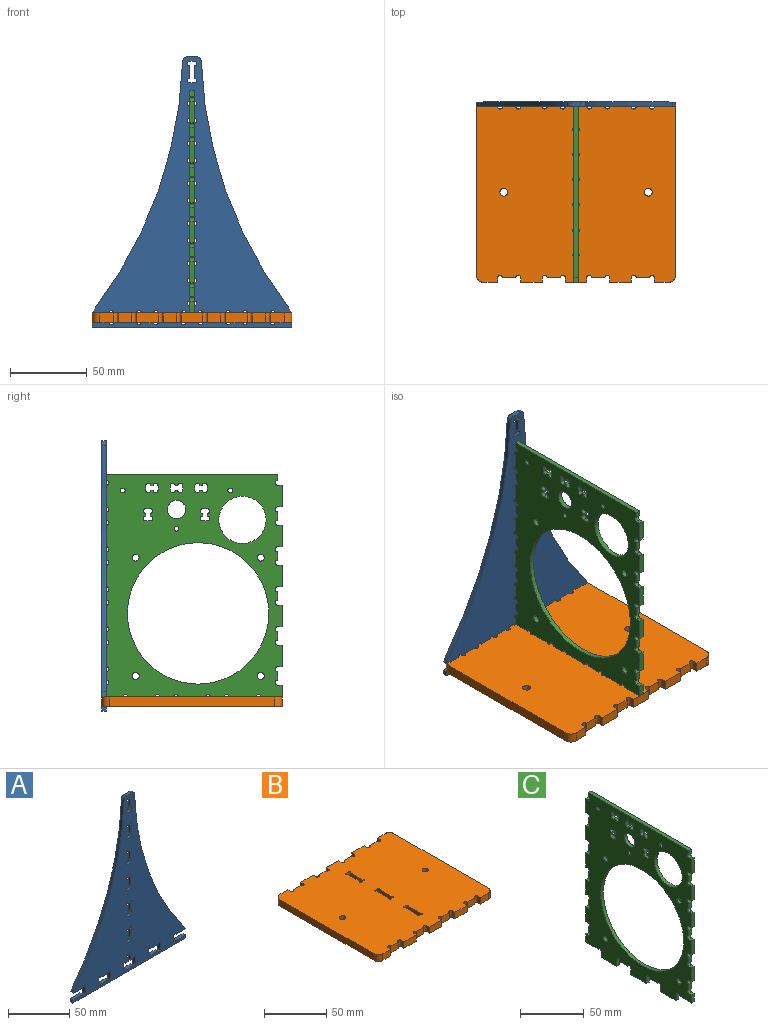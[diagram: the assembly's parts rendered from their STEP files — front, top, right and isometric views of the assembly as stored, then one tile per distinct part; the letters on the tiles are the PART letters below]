
ASSEMBLY  parts=3 mates=1
PART A: 100 faces, bbox 130x3x176 mm
  f0: plane 176x130mm, normal (0,-1,0), area 8856mm2, adj f2,f3,f4,f5,f6,f7,f8,f9
  f1: plane 176x130mm, normal (0,1,0), area 8856mm2, adj f2,f3,f4,f5,f6,f7,f8,f9
  f2: plane 3x2.5mm, normal (0,0,-1), area 7.5mm2, adj f0,f1,f19,f57
  f3: plane 11x3mm, normal (0,0,1), area 33mm2, adj f0,f1,f6,f46
  f4: plane 10.61x3mm, normal (0,0,-1), area 31.8mm2, adj f0,f1,f14,f45
  f5: cylinder r=10mm len=3.3mm, axis (0,1,0), area 11.1mm2, adj f0,f1,f9,f41
  f6: plane 3x3mm, normal (-1,0,0), area 9mm2, adj f0,f1,f3,f7
  f7: plane 130x3mm, normal (0,0,-1), area 390mm2, adj f0,f1,f6,f8
  f8: plane 3x3mm, normal (1,0,0), area 9mm2, adj f0,f1,f7,f40
  f9: cylinder r=280mm len=160.45mm, axis (0,1,0), area 518.9mm2, adj f0,f1,f5,f13
  f10: plane 6.16x3mm, normal (0,0,1), area 18.5mm2, adj f0,f1,f12,f13
  f11: cylinder r=280mm len=160.45mm, axis (0,1,0), area 518.9mm2, adj f0,f1,f12,f14
  f12: cylinder r=3mm len=3mm, axis (0,1,0), area 13.9mm2, adj f0,f1,f10,f11
  f13: cylinder r=3mm len=3mm, axis (0,1,0), area 13.9mm2, adj f0,f1,f9,f10
  f14: cylinder r=10mm len=3.3mm, axis (0,1,0), area 11.1mm2, adj f0,f1,f4,f11
  f15: plane 8x3mm, normal (0,0,1), area 24mm2, adj f0,f1,f20,f22
  f16: plane 6.35x3mm, normal (-1,0,0), area 19.1mm2, adj f0,f1,f21,f22
  f17: plane 3x2.5mm, normal (0,0,-1), area 7.5mm2, adj f0,f1,f21,f56
  f18: plane 6.35x3mm, normal (1,0,0), area 19.1mm2, adj f0,f1,f19,f20
  f19: cylinder r=1.5mm len=3mm, axis (0,-1,0), area 14.1mm2, adj f0,f1,f2,f18
  f20: cylinder r=1.5mm len=3mm, axis (0,-1,0), area 14.1mm2, adj f0,f1,f15,f18
  f21: cylinder r=1.5mm len=3mm, axis (0,-1,0), area 14.1mm2, adj f0,f1,f16,f17
  f22: cylinder r=1.5mm len=3mm, axis (0,-1,0), area 14.1mm2, adj f0,f1,f15,f16
  f23: plane 8x3mm, normal (0,0,1), area 24mm2, adj f0,f1,f28,f30
  f24: plane 6.35x3mm, normal (-1,0,0), area 19.1mm2, adj f0,f1,f29,f30
  f25: plane 8x3mm, normal (0,0,-1), area 24mm2, adj f0,f1,f27,f29
  f26: plane 6.35x3mm, normal (1,0,0), area 19.1mm2, adj f0,f1,f27,f28
  f27: cylinder r=1.5mm len=3mm, axis (0,-1,0), area 14.1mm2, adj f0,f1,f25,f26
  f28: cylinder r=1.5mm len=3mm, axis (0,-1,0), area 14.1mm2, adj f0,f1,f23,f26
  f29: cylinder r=1.5mm len=3mm, axis (0,-1,0), area 14.1mm2, adj f0,f1,f24,f25
  f30: cylinder r=1.5mm len=3mm, axis (0,-1,0), area 14.1mm2, adj f0,f1,f23,f24
  f31: plane 8x3mm, normal (0,0,1), area 24mm2, adj f0,f1,f36,f38
  f32: plane 6.35x3mm, normal (-1,0,0), area 19.1mm2, adj f0,f1,f37,f38
  f33: plane 8x3mm, normal (0,0,-1), area 24mm2, adj f0,f1,f35,f37
  f34: plane 6.35x3mm, normal (1,0,0), area 19.1mm2, adj f0,f1,f35,f36
  f35: cylinder r=1.5mm len=3mm, axis (0,-1,0), area 14.1mm2, adj f0,f1,f33,f34
  f36: cylinder r=1.5mm len=3mm, axis (0,-1,0), area 14.1mm2, adj f0,f1,f31,f34
  f37: cylinder r=1.5mm len=3mm, axis (0,-1,0), area 14.1mm2, adj f0,f1,f32,f33
  f38: cylinder r=1.5mm len=3mm, axis (0,-1,0), area 14.1mm2, adj f0,f1,f31,f32
  f39: plane 6.35x3mm, normal (1,0,0), area 19.1mm2, adj f0,f1,f42,f43
  f40: plane 11x3mm, normal (0,0,1), area 33mm2, adj f0,f1,f8,f43
  f41: plane 10.61x3mm, normal (0,0,-1), area 31.8mm2, adj f0,f1,f5,f42
  f42: cylinder r=1.5mm len=3mm, axis (0,-1,0), area 14.1mm2, adj f0,f1,f39,f41
  f43: cylinder r=1.5mm len=3mm, axis (0,-1,0), area 14.1mm2, adj f0,f1,f39,f40
  f44: plane 6.35x3mm, normal (-1,0,0), area 19.1mm2, adj f0,f1,f45,f46
  f45: cylinder r=1.5mm len=3mm, axis (0,-1,0), area 14.1mm2, adj f0,f1,f4,f44
  f46: cylinder r=1.5mm len=3mm, axis (0,-1,0), area 14.1mm2, adj f0,f1,f3,f44
  f47: plane 3x3mm, normal (0,0,1), area 9mm2, adj f0,f1,f51,f54
  f48: plane 8x3mm, normal (-1,0,0), area 24mm2, adj f0,f1,f52,f54
  f49: plane 3x3mm, normal (0,0,-1), area 9mm2, adj f0,f1,f52,f53
  f50: plane 8x3mm, normal (1,0,0), area 24mm2, adj f0,f1,f51,f53
  f51: cylinder r=1.5mm len=3mm, axis (0,-1,0), area 14.1mm2, adj f0,f1,f47,f50
  f52: cylinder r=1.5mm len=3mm, axis (0,-1,0), area 14.1mm2, adj f0,f1,f48,f49
  f53: cylinder r=1.5mm len=3mm, axis (0,-1,0), area 14.1mm2, adj f0,f1,f49,f50
  f54: cylinder r=1.5mm len=3mm, axis (0,-1,0), area 14.1mm2, adj f0,f1,f47,f48
  f55: plane 3x3mm, normal (0,0,-1), area 9mm2, adj f0,f1,f58,f59
  f56: plane 4.65x3mm, normal (-1,0,0), area 14mm2, adj f0,f1,f17,f58
  f57: plane 4.65x3mm, normal (1,0,0), area 14mm2, adj f0,f1,f2,f59
  f58: cylinder r=1.5mm len=3mm, axis (0,-1,0), area 14.1mm2, adj f0,f1,f55,f56
  f59: cylinder r=1.5mm len=3mm, axis (0,-1,0), area 14.1mm2, adj f0,f1,f55,f57
  f60: plane 3x3mm, normal (0,0,1), area 9mm2, adj f0,f1,f64,f67
  f61: plane 8x3mm, normal (-1,0,0), area 24mm2, adj f0,f1,f65,f67
  f62: plane 3x3mm, normal (0,0,-1), area 9mm2, adj f0,f1,f65,f66
  f63: plane 8x3mm, normal (1,0,0), area 24mm2, adj f0,f1,f64,f66
  f64: cylinder r=1.5mm len=3mm, axis (0,-1,0), area 14.1mm2, adj f0,f1,f60,f63
  f65: cylinder r=1.5mm len=3mm, axis (0,-1,0), area 14.1mm2, adj f0,f1,f61,f62
  f66: cylinder r=1.5mm len=3mm, axis (0,-1,0), area 14.1mm2, adj f0,f1,f62,f63
  f67: cylinder r=1.5mm len=3mm, axis (0,-1,0), area 14.1mm2, adj f0,f1,f60,f61
  f68: plane 3x3mm, normal (0,0,1), area 9mm2, adj f0,f1,f72,f75
  f69: plane 8x3mm, normal (-1,0,0), area 24mm2, adj f0,f1,f73,f75
  f70: plane 3x3mm, normal (0,0,-1), area 9mm2, adj f0,f1,f73,f74
  f71: plane 8x3mm, normal (1,0,0), area 24mm2, adj f0,f1,f72,f74
  f72: cylinder r=1.5mm len=3mm, axis (0,-1,0), area 14.1mm2, adj f0,f1,f68,f71
  f73: cylinder r=1.5mm len=3mm, axis (0,-1,0), area 14.1mm2, adj f0,f1,f69,f70
  f74: cylinder r=1.5mm len=3mm, axis (0,-1,0), area 14.1mm2, adj f0,f1,f70,f71
  f75: cylinder r=1.5mm len=3mm, axis (0,-1,0), area 14.1mm2, adj f0,f1,f68,f69
  f76: plane 3x3mm, normal (0,0,1), area 9mm2, adj f0,f1,f80,f83
  f77: plane 8x3mm, normal (-1,0,0), area 24mm2, adj f0,f1,f81,f83
  f78: plane 3x3mm, normal (0,0,-1), area 9mm2, adj f0,f1,f81,f82
  f79: plane 8x3mm, normal (1,0,0), area 24mm2, adj f0,f1,f80,f82
  f80: cylinder r=1.5mm len=3mm, axis (0,-1,0), area 14.1mm2, adj f0,f1,f76,f79
  f81: cylinder r=1.5mm len=3mm, axis (0,-1,0), area 14.1mm2, adj f0,f1,f77,f78
  f82: cylinder r=1.5mm len=3mm, axis (0,-1,0), area 14.1mm2, adj f0,f1,f78,f79
  f83: cylinder r=1.5mm len=3mm, axis (0,-1,0), area 14.1mm2, adj f0,f1,f76,f77
  f84: plane 3x3mm, normal (0,0,1), area 9mm2, adj f0,f1,f88,f91
  f85: plane 8x3mm, normal (-1,0,0), area 24mm2, adj f0,f1,f89,f91
  f86: plane 3x3mm, normal (0,0,-1), area 9mm2, adj f0,f1,f89,f90
  f87: plane 8x3mm, normal (1,0,0), area 24mm2, adj f0,f1,f88,f90
  f88: cylinder r=1.5mm len=3mm, axis (0,-1,0), area 14.1mm2, adj f0,f1,f84,f87
  f89: cylinder r=1.5mm len=3mm, axis (0,-1,0), area 14.1mm2, adj f0,f1,f85,f86
  f90: cylinder r=1.5mm len=3mm, axis (0,-1,0), area 14.1mm2, adj f0,f1,f86,f87
  f91: cylinder r=1.5mm len=3mm, axis (0,-1,0), area 14.1mm2, adj f0,f1,f84,f85
  f92: plane 3x3mm, normal (0,0,1), area 9mm2, adj f0,f1,f96,f99
  f93: plane 8x3mm, normal (-1,0,0), area 24mm2, adj f0,f1,f97,f99
  f94: plane 3x3mm, normal (0,0,-1), area 9mm2, adj f0,f1,f97,f98
  f95: plane 8x3mm, normal (1,0,0), area 24mm2, adj f0,f1,f96,f98
  f96: cylinder r=1.5mm len=3mm, axis (0,-1,0), area 14.1mm2, adj f0,f1,f92,f95
  f97: cylinder r=1.5mm len=3mm, axis (0,-1,0), area 14.1mm2, adj f0,f1,f93,f94
  f98: cylinder r=1.5mm len=3mm, axis (0,-1,0), area 14.1mm2, adj f0,f1,f94,f95
  f99: cylinder r=1.5mm len=3mm, axis (0,-1,0), area 14.1mm2, adj f0,f1,f92,f93
PART B: 84 faces, bbox 130x117.4x6.4 mm
  f0: plane 130x117.4mm, normal (0,0,1), area 14605.3mm2, adj f2,f3,f4,f5,f6,f7,f8,f9
  f1: plane 130x117.4mm, normal (0,0,-1), area 14605.3mm2, adj f2,f3,f4,f5,f6,f7,f8,f9
  f2: plane 9x6.35mm, normal (0,-1,0), area 57.1mm2, adj f0,f1,f47,f80
  f3: plane 14x6.35mm, normal (0,-1,0), area 88.9mm2, adj f0,f1,f44,f49
  f4: plane 8.65x6.35mm, normal (0,-1,0), area 54.9mm2, adj f0,f1,f42,f43
  f5: plane 8.65x6.35mm, normal (0,-1,0), area 54.9mm2, adj f0,f1,f40,f41
  f6: plane 14x6.35mm, normal (0,-1,0), area 88.9mm2, adj f0,f1,f37,f38
  f7: plane 14x6.35mm, normal (0,-1,0), area 88.9mm2, adj f0,f1,f36,f46
  f8: plane 8.65x6.35mm, normal (0,1,0), area 54.9mm2, adj f0,f1,f34,f35
  f9: plane 8.65x6.35mm, normal (0,1,0), area 54.9mm2, adj f0,f1,f32,f33
  f10: plane 9x6.35mm, normal (0,1,0), area 57.1mm2, adj f0,f1,f31,f81
  f11: plane 14x6.35mm, normal (0,1,0), area 88.9mm2, adj f0,f1,f29,f30
  f12: plane 14x6.35mm, normal (0,1,0), area 88.9mm2, adj f0,f1,f18,f23
  f13: plane 14x6.35mm, normal (0,1,0), area 88.9mm2, adj f0,f1,f20,f28
  f14: plane 9x6.35mm, normal (0,-1,0), area 57.1mm2, adj f0,f1,f39,f83
  f15: plane 107.4x6.35mm, normal (1,0,0), area 682mm2, adj f0,f1,f80,f81
  f16: plane 9x6.35mm, normal (0,1,0), area 57.1mm2, adj f0,f1,f21,f82
  f17: plane 107.4x6.35mm, normal (-1,0,0), area 682mm2, adj f0,f1,f82,f83
  f18: plane 6.35x3mm, normal (1,0,0), area 19mm2, adj f0,f1,f12,f27
  f19: plane 8.65x6.35mm, normal (0,1,0), area 54.9mm2, adj f0,f1,f26,f27
  f20: plane 6.35x3mm, normal (-1,0,0), area 19mm2, adj f0,f1,f13,f26
  f21: plane 6.35x3mm, normal (1,0,0), area 19mm2, adj f0,f1,f16,f25
  f22: plane 8.65x6.35mm, normal (0,1,0), area 54.9mm2, adj f0,f1,f24,f25
  f23: plane 6.35x3mm, normal (-1,0,0), area 19mm2, adj f0,f1,f12,f24
  f24: cylinder r=1.59mm len=6.35mm, axis (0,0,1), area 31.7mm2, adj f0,f1,f22,f23
  f25: cylinder r=1.59mm len=6.35mm, axis (0,0,1), area 31.7mm2, adj f0,f1,f21,f22
  f26: cylinder r=1.59mm len=6.35mm, axis (0,0,1), area 31.7mm2, adj f0,f1,f19,f20
  f27: cylinder r=1.59mm len=6.35mm, axis (0,0,1), area 31.7mm2, adj f0,f1,f18,f19
  f28: plane 6.35x3mm, normal (1,0,0), area 19mm2, adj f0,f1,f13,f35
  f29: plane 6.35x3mm, normal (-1,0,0), area 19mm2, adj f0,f1,f11,f34
  f30: plane 6.35x3mm, normal (1,0,0), area 19mm2, adj f0,f1,f11,f33
  f31: plane 6.35x3mm, normal (-1,0,0), area 19mm2, adj f0,f1,f10,f32
  f32: cylinder r=1.59mm len=6.35mm, axis (0,0,1), area 31.7mm2, adj f0,f1,f9,f31
  f33: cylinder r=1.59mm len=6.35mm, axis (0,0,1), area 31.7mm2, adj f0,f1,f9,f30
  f34: cylinder r=1.59mm len=6.35mm, axis (0,0,1), area 31.7mm2, adj f0,f1,f8,f29
  f35: cylinder r=1.59mm len=6.35mm, axis (0,0,1), area 31.7mm2, adj f0,f1,f8,f28
  f36: plane 6.35x3mm, normal (-1,0,0), area 19mm2, adj f0,f1,f7,f43
  f37: plane 6.35x3mm, normal (1,0,0), area 19mm2, adj f0,f1,f6,f42
  f38: plane 6.35x3mm, normal (-1,0,0), area 19mm2, adj f0,f1,f6,f41
  f39: plane 6.35x3mm, normal (1,0,0), area 19mm2, adj f0,f1,f14,f40
  f40: cylinder r=1.59mm len=6.35mm, axis (0,0,1), area 31.7mm2, adj f0,f1,f5,f39
  f41: cylinder r=1.59mm len=6.35mm, axis (0,0,1), area 31.7mm2, adj f0,f1,f5,f38
  f42: cylinder r=1.59mm len=6.35mm, axis (0,0,1), area 31.7mm2, adj f0,f1,f4,f37
  f43: cylinder r=1.59mm len=6.35mm, axis (0,0,1), area 31.7mm2, adj f0,f1,f4,f36
  f44: plane 6.35x3mm, normal (-1,0,0), area 19mm2, adj f0,f1,f3,f53
  f45: plane 8.65x6.35mm, normal (0,-1,0), area 54.9mm2, adj f0,f1,f52,f53
  f46: plane 6.35x3mm, normal (1,0,0), area 19mm2, adj f0,f1,f7,f52
  f47: plane 6.35x3mm, normal (-1,0,0), area 19mm2, adj f0,f1,f2,f51
  f48: plane 8.65x6.35mm, normal (0,-1,0), area 54.9mm2, adj f0,f1,f50,f51
  f49: plane 6.35x3mm, normal (1,0,0), area 19mm2, adj f0,f1,f3,f50
  f50: cylinder r=1.59mm len=6.35mm, axis (0,0,1), area 31.7mm2, adj f0,f1,f48,f49
  f51: cylinder r=1.59mm len=6.35mm, axis (0,0,1), area 31.7mm2, adj f0,f1,f47,f48
  f52: cylinder r=1.59mm len=6.35mm, axis (0,0,1), area 31.7mm2, adj f0,f1,f45,f46
  f53: cylinder r=1.59mm len=6.35mm, axis (0,0,1), area 31.7mm2, adj f0,f1,f44,f45
  f54: cylinder r=2.56mm len=6.35mm, axis (0,0,1), area 101.9mm2, adj f0,f1
  f55: cylinder r=2.56mm len=6.35mm, axis (0,0,1), area 101.9mm2, adj f0,f1
  f56: plane 6.35x3mm, normal (0,1,0), area 19mm2, adj f0,f1,f60,f63
  f57: plane 14.49x6.35mm, normal (-1,0,0), area 92mm2, adj f0,f1,f62,f63
  f58: plane 6.35x3mm, normal (0,-1,0), area 19mm2, adj f0,f1,f61,f62
  f59: plane 14.49x6.35mm, normal (1,0,0), area 92mm2, adj f0,f1,f60,f61
  f60: cylinder r=0.79mm len=6.35mm, axis (0,0,1), area 15.8mm2, adj f0,f1,f56,f59
  f61: cylinder r=0.79mm len=6.35mm, axis (0,0,1), area 15.8mm2, adj f0,f1,f58,f59
  f62: cylinder r=0.79mm len=6.35mm, axis (0,0,1), area 15.8mm2, adj f0,f1,f57,f58
  f63: cylinder r=0.79mm len=6.35mm, axis (0,0,1), area 15.8mm2, adj f0,f1,f56,f57
  f64: plane 6.35x3mm, normal (0,1,0), area 19mm2, adj f0,f1,f68,f71
  f65: plane 14.49x6.35mm, normal (-1,0,0), area 92mm2, adj f0,f1,f70,f71
  f66: plane 6.35x3mm, normal (0,-1,0), area 19mm2, adj f0,f1,f69,f70
  f67: plane 14.49x6.35mm, normal (1,0,0), area 92mm2, adj f0,f1,f68,f69
  f68: cylinder r=0.79mm len=6.35mm, axis (0,0,1), area 15.8mm2, adj f0,f1,f64,f67
  f69: cylinder r=0.79mm len=6.35mm, axis (0,0,1), area 15.8mm2, adj f0,f1,f66,f67
  f70: cylinder r=0.79mm len=6.35mm, axis (0,0,1), area 15.8mm2, adj f0,f1,f65,f66
  f71: cylinder r=0.79mm len=6.35mm, axis (0,0,1), area 15.8mm2, adj f0,f1,f64,f65
  f72: plane 6.35x3mm, normal (0,1,0), area 19mm2, adj f0,f1,f76,f79
  f73: plane 14.49x6.35mm, normal (-1,0,0), area 92mm2, adj f0,f1,f78,f79
  f74: plane 6.35x3mm, normal (0,-1,0), area 19mm2, adj f0,f1,f77,f78
  f75: plane 14.49x6.35mm, normal (1,0,0), area 92mm2, adj f0,f1,f76,f77
  f76: cylinder r=0.79mm len=6.35mm, axis (0,0,1), area 15.8mm2, adj f0,f1,f72,f75
  f77: cylinder r=0.79mm len=6.35mm, axis (0,0,1), area 15.8mm2, adj f0,f1,f74,f75
  f78: cylinder r=0.79mm len=6.35mm, axis (0,0,1), area 15.8mm2, adj f0,f1,f73,f74
  f79: cylinder r=0.79mm len=6.35mm, axis (0,0,1), area 15.8mm2, adj f0,f1,f72,f73
  f80: cylinder r=5mm len=6.35mm, axis (0,0,1), area 49.9mm2, adj f0,f1,f2,f15
  f81: cylinder r=5mm len=6.35mm, axis (0,0,-1), area 49.9mm2, adj f0,f1,f10,f15
  f82: cylinder r=5mm len=6.35mm, axis (0,0,1), area 49.9mm2, adj f0,f1,f16,f17
  f83: cylinder r=5mm len=6.35mm, axis (0,0,-1), area 49.9mm2, adj f0,f1,f14,f17
PART C: 142 faces, bbox 3x117.4x151 mm
  f0: plane 151x117.4mm, normal (1,0,0), area 9013.7mm2, adj f2,f3,f4,f5,f6,f7,f8,f9
  f1: plane 151x117.4mm, normal (-1,0,0), area 9013.7mm2, adj f2,f3,f4,f5,f6,f7,f8,f9
  f2: plane 8.8x3mm, normal (0,0,-1), area 26.4mm2, adj f0,f1,f87,f88
  f3: plane 13.88x3mm, normal (0,0,-1), area 41.6mm2, adj f0,f1,f6,f86
  f4: plane 17.67x3mm, normal (0,0,-1), area 53mm2, adj f0,f1,f83,f85
  f5: plane 17.67x3mm, normal (0,0,-1), area 53mm2, adj f0,f1,f76,f84
  f6: plane 7.65x3mm, normal (0,1,0), area 23mm2, adj f0,f1,f3,f60
  f7: plane 17.67x3mm, normal (0,0,-1), area 53mm2, adj f0,f1,f75,f79
  f8: plane 7.65x3mm, normal (0,-1,0), area 23mm2, adj f0,f1,f48,f78
  f9: plane 14x3mm, normal (0,1,0), area 42mm2, adj f0,f1,f42,f66
  f10: plane 14x3mm, normal (0,1,0), area 42mm2, adj f0,f1,f63,f68
  f11: plane 14x3mm, normal (0,1,0), area 42mm2, adj f0,f1,f61,f65
  f12: plane 5.65x3mm, normal (0,-1,0), area 17mm2, adj f0,f1,f58,f59
  f13: plane 5.65x3mm, normal (0,-1,0), area 17mm2, adj f0,f1,f56,f57
  f14: plane 5.65x3mm, normal (0,-1,0), area 17mm2, adj f0,f1,f54,f55
  f15: plane 14x3mm, normal (0,-1,0), area 42mm2, adj f0,f1,f30,f53
  f16: plane 14x3mm, normal (0,-1,0), area 42mm2, adj f0,f1,f51,f52
  f17: plane 14x3mm, normal (0,-1,0), area 42mm2, adj f0,f1,f49,f50
  f18: plane 3.83x3mm, normal (0,1,0), area 11.5mm2, adj f0,f1,f47,f139
  f19: plane 5.65x3mm, normal (0,1,0), area 17mm2, adj f0,f1,f45,f46
  f20: plane 5.65x3mm, normal (0,1,0), area 17mm2, adj f0,f1,f43,f44
  f21: plane 14x3mm, normal (0,1,0), area 42mm2, adj f0,f1,f40,f41
  f22: plane 14x3mm, normal (0,1,0), area 42mm2, adj f0,f1,f38,f39
  f23: plane 14x3mm, normal (0,-1,0), area 42mm2, adj f0,f1,f27,f32
  f24: plane 14x3mm, normal (0,-1,0), area 42mm2, adj f0,f1,f25,f29
  f25: plane 3x3mm, normal (0,0,1), area 9mm2, adj f0,f1,f24,f37
  f26: plane 3.83x3mm, normal (0,-1,0), area 11.5mm2, adj f0,f1,f37,f139
  f27: plane 3x3mm, normal (0,0,1), area 9mm2, adj f0,f1,f23,f36
  f28: plane 5.65x3mm, normal (0,-1,0), area 17mm2, adj f0,f1,f35,f36
  f29: plane 3x3mm, normal (0,0,-1), area 9mm2, adj f0,f1,f24,f35
  f30: plane 3x3mm, normal (0,0,1), area 9mm2, adj f0,f1,f15,f34
  f31: plane 5.65x3mm, normal (0,-1,0), area 17mm2, adj f0,f1,f33,f34
  f32: plane 3x3mm, normal (0,0,-1), area 9mm2, adj f0,f1,f23,f33
  f33: cylinder r=1.59mm len=3.18mm, axis (1,0,0), area 15mm2, adj f0,f1,f31,f32
  f34: cylinder r=1.59mm len=3.18mm, axis (1,0,0), area 15mm2, adj f0,f1,f30,f31
  f35: cylinder r=1.59mm len=3.18mm, axis (1,0,0), area 15mm2, adj f0,f1,f28,f29
  f36: cylinder r=1.59mm len=3.18mm, axis (1,0,0), area 15mm2, adj f0,f1,f27,f28
  f37: cylinder r=1.59mm len=3.18mm, axis (1,0,0), area 15mm2, adj f0,f1,f25,f26
  f38: plane 3x3mm, normal (0,0,1), area 9mm2, adj f0,f1,f22,f47
  f39: plane 3x3mm, normal (0,0,-1), area 9mm2, adj f0,f1,f22,f46
  f40: plane 3x3mm, normal (0,0,1), area 9mm2, adj f0,f1,f21,f45
  f41: plane 3x3mm, normal (0,0,-1), area 9mm2, adj f0,f1,f21,f44
  f42: plane 3x3mm, normal (0,0,1), area 9mm2, adj f0,f1,f9,f43
  f43: cylinder r=1.59mm len=3.18mm, axis (1,0,0), area 15mm2, adj f0,f1,f20,f42
  f44: cylinder r=1.59mm len=3.18mm, axis (1,0,0), area 15mm2, adj f0,f1,f20,f41
  f45: cylinder r=1.59mm len=3.18mm, axis (1,0,0), area 15mm2, adj f0,f1,f19,f40
  f46: cylinder r=1.59mm len=3.18mm, axis (1,0,0), area 15mm2, adj f0,f1,f19,f39
  f47: cylinder r=1.59mm len=3.18mm, axis (1,0,0), area 15mm2, adj f0,f1,f18,f38
  f48: plane 3x3mm, normal (0,0,1), area 9mm2, adj f0,f1,f8,f59
  f49: plane 3x3mm, normal (0,0,-1), area 9mm2, adj f0,f1,f17,f58
  f50: plane 3x3mm, normal (0,0,1), area 9mm2, adj f0,f1,f17,f57
  f51: plane 3x3mm, normal (0,0,-1), area 9mm2, adj f0,f1,f16,f56
  f52: plane 3x3mm, normal (0,0,1), area 9mm2, adj f0,f1,f16,f55
  f53: plane 3x3mm, normal (0,0,-1), area 9mm2, adj f0,f1,f15,f54
  f54: cylinder r=1.59mm len=3.18mm, axis (1,0,0), area 15mm2, adj f0,f1,f14,f53
  f55: cylinder r=1.59mm len=3.18mm, axis (1,0,0), area 15mm2, adj f0,f1,f14,f52
  f56: cylinder r=1.59mm len=3.18mm, axis (1,0,0), area 15mm2, adj f0,f1,f13,f51
  f57: cylinder r=1.59mm len=3.18mm, axis (1,0,0), area 15mm2, adj f0,f1,f13,f50
  f58: cylinder r=1.59mm len=3.18mm, axis (1,0,0), area 15mm2, adj f0,f1,f12,f49
  f59: cylinder r=1.59mm len=3.18mm, axis (1,0,0), area 15mm2, adj f0,f1,f12,f48
  f60: plane 3x3mm, normal (0,0,1), area 9mm2, adj f0,f1,f6,f74
  f61: plane 3x3mm, normal (0,0,-1), area 9mm2, adj f0,f1,f11,f73
  f62: plane 5.65x3mm, normal (0,1,0), area 17mm2, adj f0,f1,f73,f74
  f63: plane 3x3mm, normal (0,0,-1), area 9mm2, adj f0,f1,f10,f72
  f64: plane 5.65x3mm, normal (0,1,0), area 17mm2, adj f0,f1,f71,f72
  f65: plane 3x3mm, normal (0,0,1), area 9mm2, adj f0,f1,f11,f71
  f66: plane 3x3mm, normal (0,0,-1), area 9mm2, adj f0,f1,f9,f70
  f67: plane 5.65x3mm, normal (0,1,0), area 17mm2, adj f0,f1,f69,f70
  f68: plane 3x3mm, normal (0,0,1), area 9mm2, adj f0,f1,f10,f69
  f69: cylinder r=1.59mm len=3.18mm, axis (1,0,0), area 15mm2, adj f0,f1,f67,f68
  f70: cylinder r=1.59mm len=3.18mm, axis (1,0,0), area 15mm2, adj f0,f1,f66,f67
  f71: cylinder r=1.59mm len=3.18mm, axis (1,0,0), area 15mm2, adj f0,f1,f64,f65
  f72: cylinder r=1.59mm len=3.18mm, axis (1,0,0), area 15mm2, adj f0,f1,f63,f64
  f73: cylinder r=1.59mm len=3.18mm, axis (1,0,0), area 15mm2, adj f0,f1,f61,f62
  f74: cylinder r=1.59mm len=3.18mm, axis (1,0,0), area 15mm2, adj f0,f1,f60,f62
  f75: plane 6.35x3mm, normal (0,1,0), area 19.1mm2, adj f0,f1,f7,f82
  f76: plane 6.35x3mm, normal (0,-1,0), area 19.1mm2, adj f0,f1,f5,f81
  f77: plane 8.8x3mm, normal (0,0,-1), area 26.4mm2, adj f0,f1,f81,f82
  f78: plane 13.88x3mm, normal (0,0,-1), area 41.6mm2, adj f0,f1,f8,f80
  f79: plane 6.35x3mm, normal (0,-1,0), area 19.1mm2, adj f0,f1,f7,f80
  f80: cylinder r=1.59mm len=3.18mm, axis (1,0,0), area 15mm2, adj f0,f1,f78,f79
  f81: cylinder r=1.59mm len=3.18mm, axis (1,0,0), area 15mm2, adj f0,f1,f76,f77
  f82: cylinder r=1.59mm len=3.18mm, axis (1,0,0), area 15mm2, adj f0,f1,f75,f77
  f83: plane 6.35x3mm, normal (0,-1,0), area 19.1mm2, adj f0,f1,f4,f88
  f84: plane 6.35x3mm, normal (0,1,0), area 19.1mm2, adj f0,f1,f5,f87
  f85: plane 6.35x3mm, normal (0,1,0), area 19.1mm2, adj f0,f1,f4,f86
  f86: cylinder r=1.59mm len=3.18mm, axis (1,0,0), area 15mm2, adj f0,f1,f3,f85
  f87: cylinder r=1.59mm len=3.18mm, axis (1,0,0), area 15mm2, adj f0,f1,f2,f84
  f88: cylinder r=1.59mm len=3.18mm, axis (1,0,0), area 15mm2, adj f0,f1,f2,f83
  f89: cylinder r=46mm len=92mm, axis (1,0,0), area 867.1mm2, adj f0,f1
  f90: cylinder r=2.3mm len=4.6mm, axis (1,0,0), area 43.4mm2, adj f0,f1
  f91: cylinder r=2.3mm len=4.6mm, axis (1,0,0), area 43.4mm2, adj f0,f1
  f92: cylinder r=2.3mm len=4.6mm, axis (1,0,0), area 43.4mm2, adj f0,f1
  f93: cylinder r=2.3mm len=4.6mm, axis (1,0,0), area 43.4mm2, adj f0,f1
  f94: cylinder r=1.59mm len=3.18mm, axis (1,0,0), area 29.9mm2, adj f0,f1
  f95: cylinder r=1.59mm len=3.18mm, axis (1,0,0), area 29.9mm2, adj f0,f1
  f96: cylinder r=1.59mm len=3.18mm, axis (1,0,0), area 29.9mm2, adj f0,f1
  f97: cylinder r=1.59mm len=3.18mm, axis (1,0,0), area 15mm2, adj f0,f1,f98,f104
  f98: plane 3x1.65mm, normal (0,1,0), area 4.9mm2, adj f0,f1,f97,f99
  f99: cylinder r=1.59mm len=3.18mm, axis (1,0,0), area 15mm2, adj f0,f1,f98,f100
  f100: plane 3x3mm, normal (0,0,1), area 9mm2, adj f0,f1,f99,f101
  f101: cylinder r=1.59mm len=3.18mm, axis (1,0,0), area 15mm2, adj f0,f1,f100,f102
  f102: plane 3x1.65mm, normal (0,-1,0), area 4.9mm2, adj f0,f1,f101,f103
  f103: cylinder r=1.59mm len=3.18mm, axis (1,0,0), area 15mm2, adj f0,f1,f102,f104
  f104: plane 3x3mm, normal (0,0,-1), area 9mm2, adj f0,f1,f97,f103
  f105: cylinder r=1.59mm len=3.18mm, axis (1,0,0), area 15mm2, adj f0,f1,f106,f112
  f106: plane 3x1.65mm, normal (0,0,1), area 4.9mm2, adj f0,f1,f105,f107
  f107: cylinder r=1.59mm len=3.18mm, axis (1,0,0), area 15mm2, adj f0,f1,f106,f108
  f108: plane 3x3mm, normal (0,-1,0), area 9mm2, adj f0,f1,f107,f109
  f109: cylinder r=1.59mm len=3.18mm, axis (1,0,0), area 15mm2, adj f0,f1,f108,f110
  f110: plane 3x1.65mm, normal (0,0,-1), area 4.9mm2, adj f0,f1,f109,f111
  f111: cylinder r=1.59mm len=3.18mm, axis (1,0,0), area 15mm2, adj f0,f1,f110,f112
  f112: plane 3x3mm, normal (0,1,0), area 9mm2, adj f0,f1,f105,f111
  f113: cylinder r=1.59mm len=3.18mm, axis (1,0,0), area 15mm2, adj f0,f1,f114,f120
  f114: plane 3x1.65mm, normal (0,0,1), area 4.9mm2, adj f0,f1,f113,f115
  f115: cylinder r=1.59mm len=3.18mm, axis (1,0,0), area 15mm2, adj f0,f1,f114,f116
  f116: plane 3x3mm, normal (0,-1,0), area 9mm2, adj f0,f1,f115,f117
  f117: cylinder r=1.59mm len=3.18mm, axis (1,0,0), area 15mm2, adj f0,f1,f116,f118
  f118: plane 3x1.65mm, normal (0,0,-1), area 4.9mm2, adj f0,f1,f117,f119
  f119: cylinder r=1.59mm len=3.18mm, axis (1,0,0), area 15mm2, adj f0,f1,f118,f120
  f120: plane 3x3mm, normal (0,1,0), area 9mm2, adj f0,f1,f113,f119
  f121: plane 3x0mm, normal (0,-1,0), area 0mm2, adj f0,f1,f122,f130
  f122: plane 3x1.65mm, normal (0,0,1), area 4.9mm2, adj f0,f1,f121,f123
  f123: cylinder r=1.59mm len=3.18mm, axis (1,0,0), area 15mm2, adj f0,f1,f122,f124
  f124: plane 3x3mm, normal (0,-1,0), area 9mm2, adj f0,f1,f123,f125
  f125: cylinder r=1.59mm len=3.18mm, axis (1,0,0), area 15mm2, adj f0,f1,f124,f126
  f126: plane 3x0mm, normal (0,1,0), area 0mm2, adj f0,f1,f125,f127
  f127: plane 3x1.65mm, normal (0,0,-1), area 4.9mm2, adj f0,f1,f126,f128
  f128: cylinder r=1.59mm len=3.18mm, axis (1,0,0), area 15mm2, adj f0,f1,f127,f129
  f129: plane 3x3mm, normal (0,1,0), area 9mm2, adj f0,f1,f128,f130
  f130: cylinder r=1.59mm len=3.18mm, axis (1,0,0), area 15mm2, adj f0,f1,f121,f129
  f131: cylinder r=1.59mm len=3.18mm, axis (1,0,0), area 15mm2, adj f0,f1,f132,f138
  f132: plane 3x1.65mm, normal (0,1,0), area 4.9mm2, adj f0,f1,f131,f133
  f133: cylinder r=1.59mm len=3.18mm, axis (1,0,0), area 15mm2, adj f0,f1,f132,f134
  f134: plane 3x3mm, normal (0,0,1), area 9mm2, adj f0,f1,f133,f135
  f135: cylinder r=1.59mm len=3.18mm, axis (1,0,0), area 15mm2, adj f0,f1,f134,f136
  f136: plane 3x1.65mm, normal (0,-1,0), area 4.9mm2, adj f0,f1,f135,f137
  f137: cylinder r=1.59mm len=3.18mm, axis (1,0,0), area 15mm2, adj f0,f1,f136,f138
  f138: plane 3x3mm, normal (0,0,-1), area 9mm2, adj f0,f1,f131,f137
  f139: plane 111.4x3mm, normal (0,0,1), area 334.2mm2, adj f0,f1,f18,f26
  f140: cylinder r=6mm len=12mm, axis (1,0,0), area 113.1mm2, adj f0,f1
  f141: cylinder r=15.37mm len=30.73mm, axis (1,0,0), area 289.6mm2, adj f0,f1
PLACE A t=(-40.56,65.81,45.79)mm
PLACE B t=(-40.56,7.11,-39.21)mm
PLACE C t=(-42.06,7.11,45.79)mm
MATE fastened B.f0 <-> C.f78  axis (0,0,1) through (-39.06,-34.54,-32.86)mm
